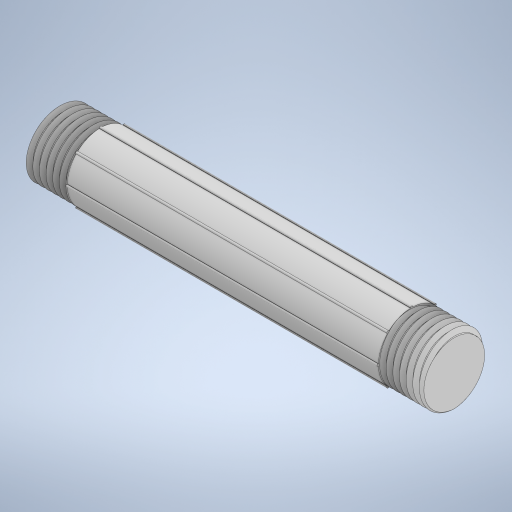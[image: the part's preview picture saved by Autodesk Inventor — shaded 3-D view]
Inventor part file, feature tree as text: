
AUTODESK INVENTOR PART (.ipt)
format: ipt  version: 2024 (Build 280153000, 153)  size: 547,840 bytes
history: native  units: mm
features: sketch x4, extrude x3, mirror x2, other x1, pattern_circular x1, fillet x1
ambient origin geometry x8: Origin, YZ Plane, XZ Plane, XY Plane, X Axis, Y Axis, Z Axis, Center Point
bodies: Body1 (feature_tree)
feature tree (12):
  extrude  "Base"  Depth=83.7mm TaperAngle=0.0deg
  other  "Spirale2"
  mirror  "Spiegeln1"
  extrude  "Extrusion14"  TaperAngle=60.0deg  [1 undecoded]
  extrude  "Extrusion15"  Depth=65.7mm TaperAngle=0.0deg
  mirror  "Spiegeln2"
  pattern_circular  "Runde Anordnung3"  [2 undecoded]
  fillet  "Rundung7"  Radius=0.3mm
  sketch  "Skizze21"  dims[d97=14.0mm d98=83.7mm d99=0.0mm]
  sketch  "Skizze22"  dims[d100=1.4mm d101=60.0deg]
  sketch  "Skizze23"  dims[d102=0.2mm]
  sketch  "Skizze25"  dims[d103=1.4mm d104=10.9mm d105=10.0mm d106=0.0mm d107=90.0deg d108=90.0deg d109=0.0mm d110=0.0mm d111=65.7mm d112=0.0mm d113=14.0mm d114=0.3mm d115=0.24mm d116=65.7mm d117=0.0mm d118=0.24mm d119=80.0mm d120=360.0deg d52=0.0mm d53=0.0mm d54=0.0mm d55=0.0mm]
note: 3 required parameter values undecoded (feature->parameter linkage not recoverable at this tier; creation-order binding heuristic only, values carry confidence <= 0.55)
